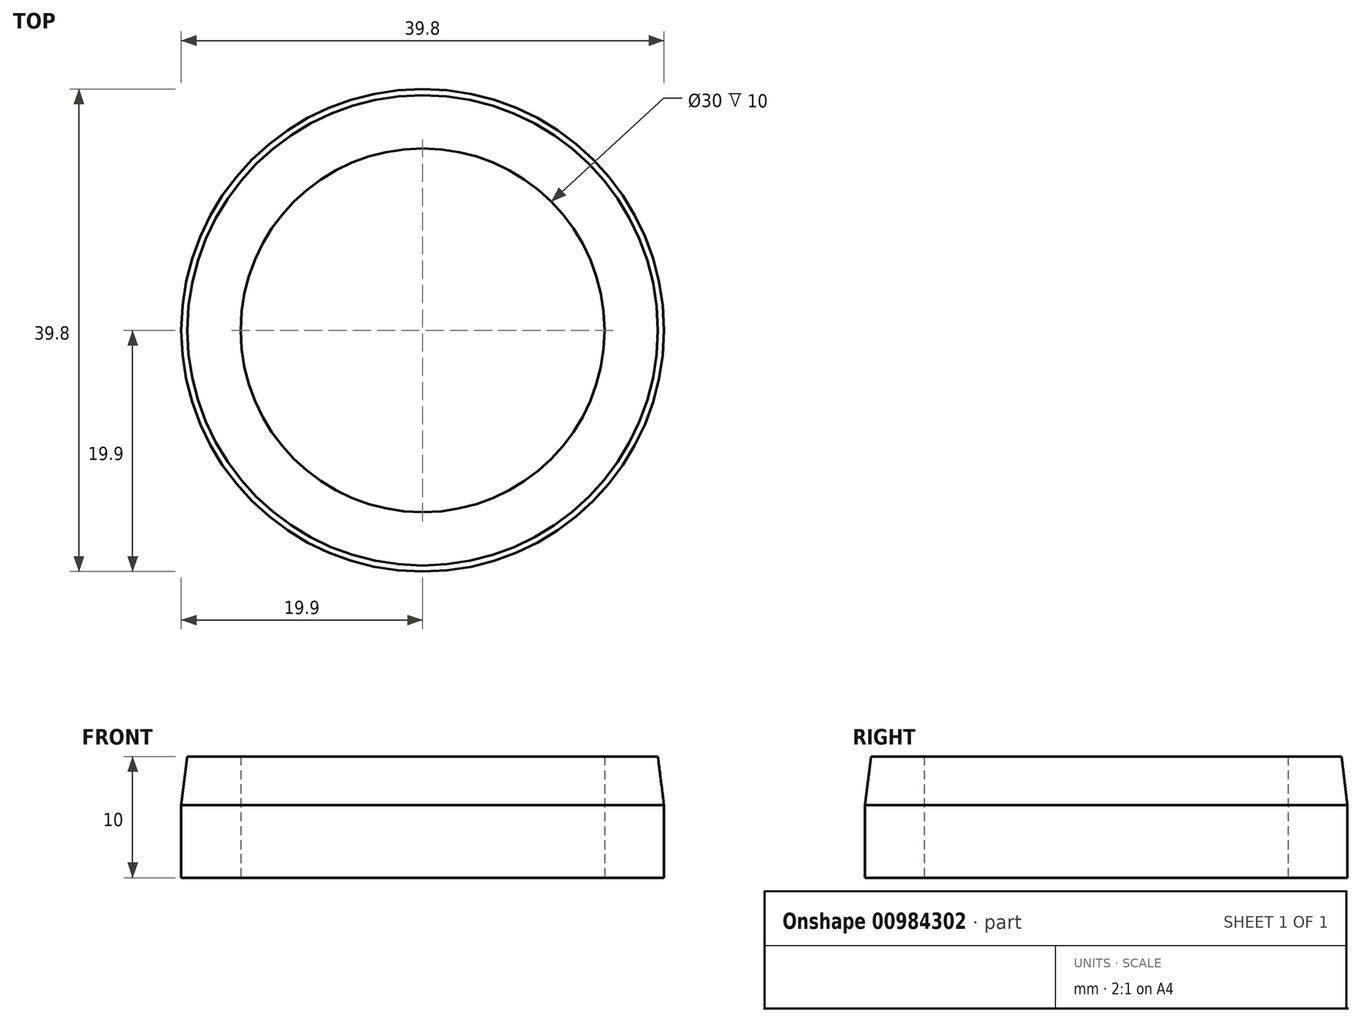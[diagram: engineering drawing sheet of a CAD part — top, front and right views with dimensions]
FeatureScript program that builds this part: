
annotation { "Feature Type Name" : "Feature", "Feature Type Description" : "" }
export const myFeature = defineFeature(function(context is Context, id is Id, definition is map)
    precondition{}
    {
        {
            var Q0;
            Q0=qCreatedBy(makeId("Top.planeOp"),FACE);
            var sketch = newSketch(context, id + "F0", { "sketchPlane" : qUnion([Q0])});
            skCircle(sketch, "E0", {"center": v(0, 0) * mm, "radius": 15 * mm});
            skCircle(sketch, "E1", {"center": v(0, 0) * mm, "radius": 19.9 * mm});
            skSolve(sketch);
        }
        {
            var Q0;
            Q0 = qSketchRegion(id + "F0", true);
            extrude(context, id + "F1", {"entities" : qUnion([Q0]), "depth" : 10 * mm, "offsetDistance" : 25 * mm});
        }
        {
            var Q0;
            Q0=makeQuery(id+"F1.opExtrude","CAP_EDGE",EDGE,{"disambiguationData":[OSD([sQuery(id+"F0.wireOp",EDGE,"E1")])],"isStart":false});
            chamfer(context, id + "F2", {"entities" : qUnion([Q0]), "chamferType" : ChamferType.TWO_OFFSETS, "width1" : 0.5 * mm, "oppositeDirection" : false, "width2" : 4 * mm, "tangentPropagation" : true});
        }
    });
